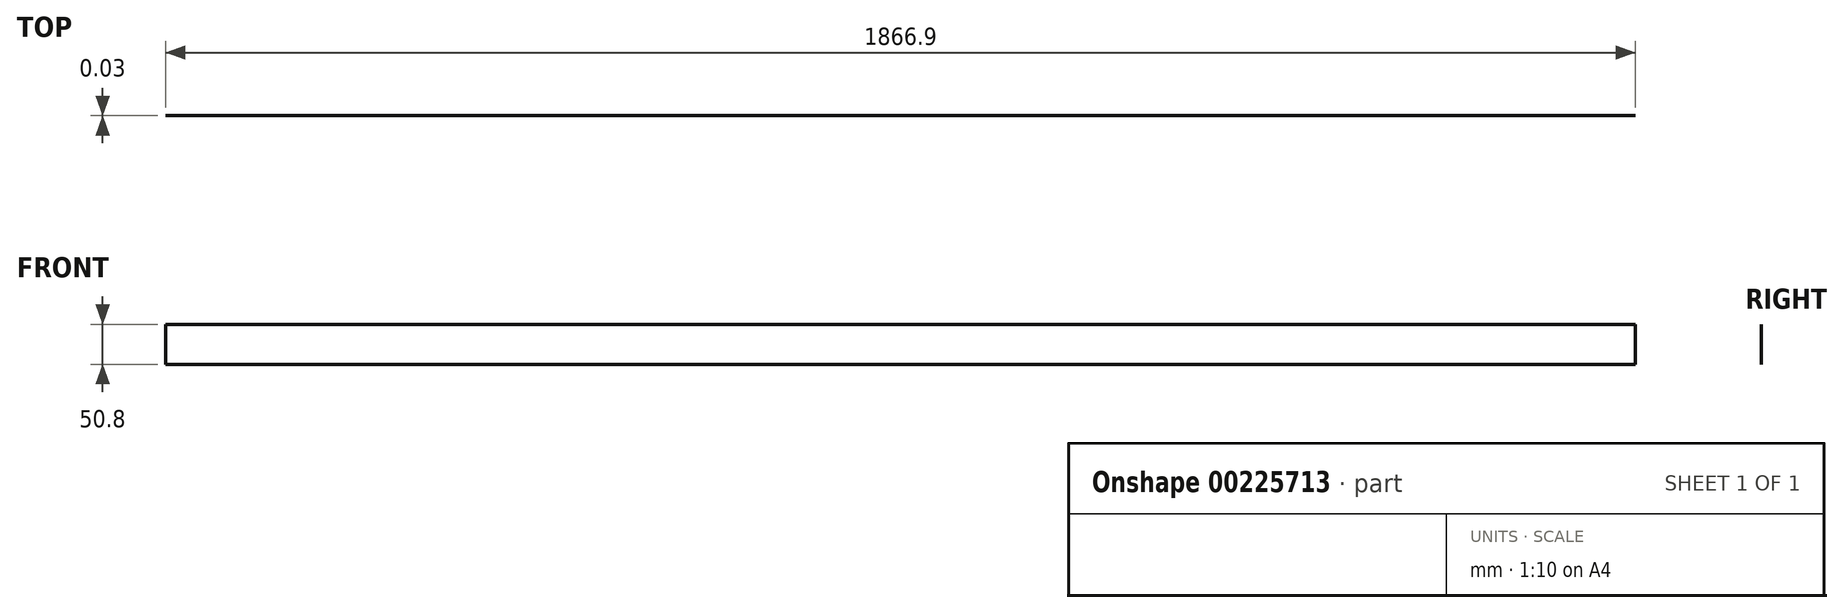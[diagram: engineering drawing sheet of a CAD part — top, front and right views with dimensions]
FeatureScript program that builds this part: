
annotation { "Feature Type Name" : "Feature", "Feature Type Description" : "" }
export const myFeature = defineFeature(function(context is Context, id is Id, definition is map)
    precondition{}
    {
        {
            var Q0;
            Q0=qCreatedBy(makeId("Front.planeOp"),FACE);
            var sketch = newSketch(context, id + "F0", { "sketchPlane" : qUnion([Q0])});
            skLineSegment(sketch, "E0.bottom", {"start": v(-111.13, 38.14) * mm, "end": v(1755.77, 38.14) * mm});
            skLineSegment(sketch, "E0.top", {"start": v(-111.13, -12.66) * mm, "end": v(1755.77, -12.66) * mm});
            skLineSegment(sketch, "E0.left", {"start": v(-111.13, 38.14) * mm, "end": v(-111.13, -12.66) * mm});
            skLineSegment(sketch, "E0.right", {"start": v(1755.77, 38.14) * mm, "end": v(1755.77, -12.66) * mm});
            skSolve(sketch);
        }
        {
            var Q0;
            Q0=makeQuery(id+"F0.imprint","IMPRINT",FACE,{"disambiguationData":[TD([[makeQuery(id+"F0.imprint","IMPRINT",EDGE,{"derivedFrom":sQuery(id+"F0.wireOp",EDGE,"E0.bottom")}),-1.0]])]});
            extrude(context, id + "F1", {"entities" : qUnion([Q0]), "depth" : 23 / 812.8 * mm});
        }
    });
